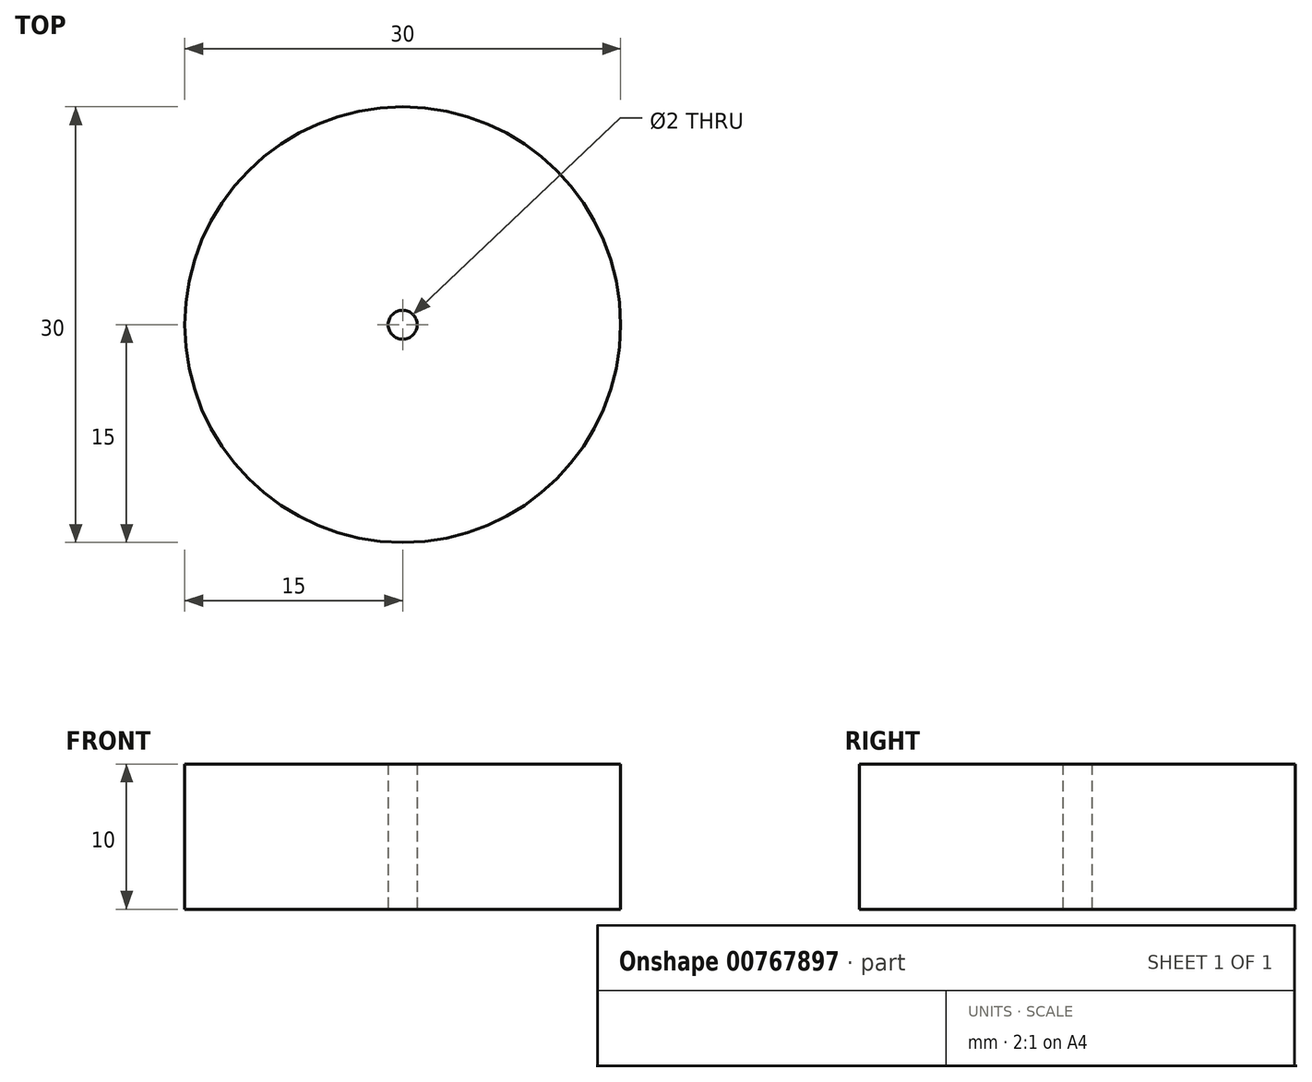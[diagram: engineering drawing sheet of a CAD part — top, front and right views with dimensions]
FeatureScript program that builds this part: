
annotation { "Feature Type Name" : "Feature", "Feature Type Description" : "" }
export const myFeature = defineFeature(function(context is Context, id is Id, definition is map)
    precondition{}
    {
        {
            var Q0;
            Q0=qCreatedBy(makeId("Top.planeOp"),FACE);
            var sketch = newSketch(context, id + "F0", { "sketchPlane" : qUnion([Q0])});
            skCircle(sketch, "E0", {"center": v(0, 0) * mm, "radius": 15 * mm});
            skCircle(sketch, "E1", {"center": v(0, 0) * mm, "radius": 1 * mm});
            skSolve(sketch);
        }
        {
            var Q0;
            Q0 = qSketchRegion(id + "F0", true);
            extrude(context, id + "F1", {"entities" : qUnion([Q0]), "depth" : 10 * mm, "offsetDistance" : 25 * mm});
        }
    });
